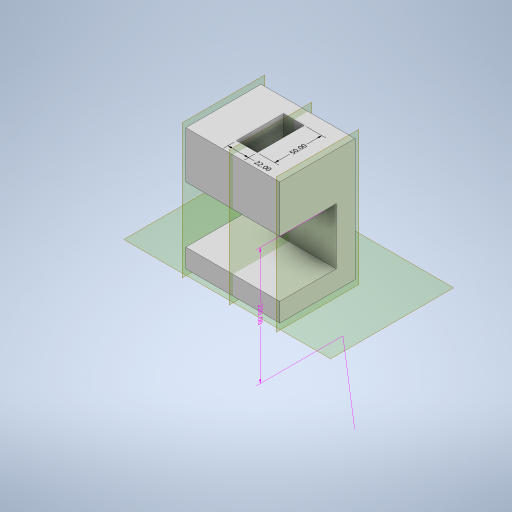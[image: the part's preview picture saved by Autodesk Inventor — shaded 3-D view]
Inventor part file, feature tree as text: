
AUTODESK INVENTOR PART (.ipt)
format: ipt  version: 2023 (Build 270158000, 158)  size: 342,528 bytes
history: native  units: mm
features: other x7, extrude x6, plane x6, sketch x6, split x3
ambient origin geometry x8: Origin, YZ Plane, XZ Plane, XY Plane, X Axis, Y Axis, Z Axis, Center Point
bodies: Body1 (feature_tree), Body2 (feature_tree)
feature tree (28):
  other  "Sólido1"
  other  "Anotaciones"
  extrude  "Extrusión1"  Depth=80.0mm
  extrude  "Extrusión2"  Depth=130.0mm
  extrude  "Extrusión3"  Depth=20.0mm
  extrude  "Extrusión4"  Depth=43.0mm TaperAngle=0.0deg
  plane  "Plano de trabajo1"
  extrude  "Extrusión6"  Depth=20.0mm TaperAngle=0.0deg
  plane  "Plano de trabajo3"
  extrude  "Extrusión7"  Depth=50.0mm TaperAngle=0.0deg
  plane  "Plano de trabajo4"
  split  "Dividir1"
  other  "Suprimir cara4"
  plane  "Plano de trabajo5"
  plane  "Plano de trabajo6"
  plane  "Plano de trabajo7"
  split  "Dividir2"
  split  "Dividir3"
  sketch  "Boceto1"  dims[d0=200.0mm d1=80.0mm]
  sketch  "Boceto2"  dims[d2=130.0mm d3=0.0mm d4=180.0mm]
  sketch  "Boceto3"  dims[d5=60.0mm d6=20.0mm]
  sketch  "Boceto4"  dims[d7=60.0mm d8=0.0mm d11=43.0mm d12=0.0mm]
  sketch  "Boceto7"  dims[d13=20.0mm d14=90.0mm d15=0.0mm]
  other  "Sólido3"
  sketch  "Boceto10"  dims[d16=-90.0mm d28=20.0mm d29=20.0mm d30=30.0mm d31=30.0mm d32=20.0mm d33=35.0mm d34=35.0mm d35=69.0mm d36=10.0mm d37=0.0mm d45=1.5mm d50=10.0mm d51=0.0mm d52=10.0mm d54=90.0deg d62=22.0mm d63=50.0mm d38=3.166395mm d39=4.283575mm d40=220.0mm d64=7.612463mm d65=1.70839mm d66=22.0mm d67=2.659054mm d68=7.748512mm d69=50.0mm]
  other  "Cota lineal 1"
  other  "Cota lineal 2"
  other  "Cota lineal 3"
